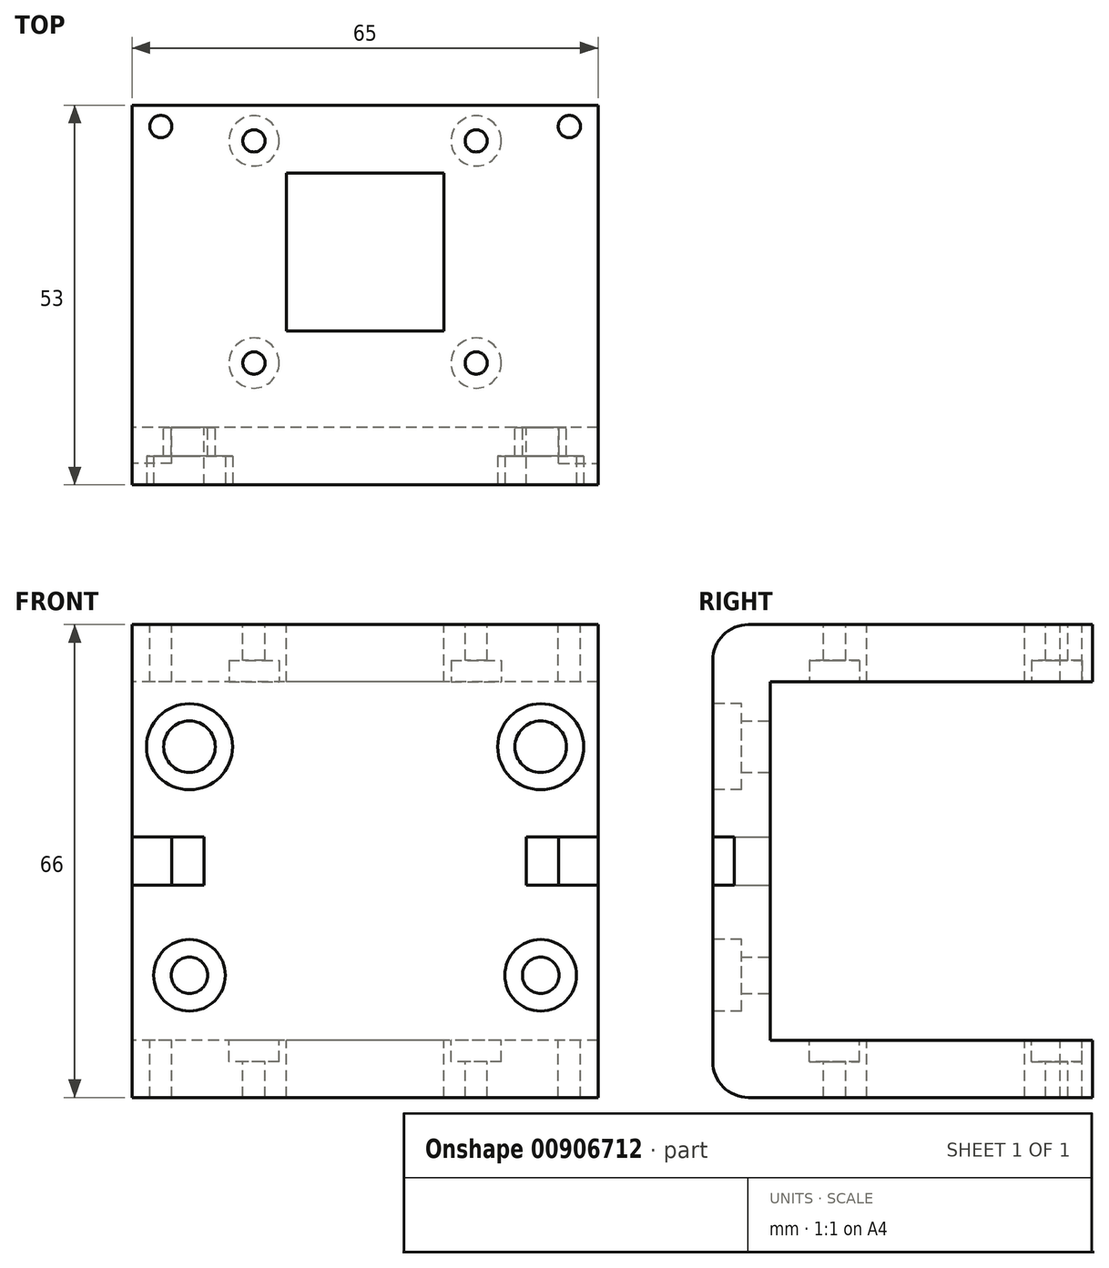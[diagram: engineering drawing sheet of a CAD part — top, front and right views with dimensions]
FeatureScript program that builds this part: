
annotation { "Feature Type Name" : "Feature", "Feature Type Description" : "" }
export const myFeature = defineFeature(function(context is Context, id is Id, definition is map)
    precondition{}
    {
        {
            var Q0;
            Q0=qCreatedBy(makeId("Front.planeOp"),FACE);
            var sketch = newSketch(context, id + "F0", { "sketchPlane" : qUnion([Q0])});
            skLineSegment(sketch, "E0.bottom", {"start": v(-32.5, 25) * mm, "end": v(32.5, 25) * mm});
            skLineSegment(sketch, "E0.top", {"start": v(-32.5, -25) * mm, "end": v(32.5, -25) * mm});
            skLineSegment(sketch, "E0.left", {"start": v(-32.5, 25) * mm, "end": v(-32.5, -25) * mm});
            skLineSegment(sketch, "E0.right", {"start": v(32.5, 25) * mm, "end": v(32.5, -25) * mm});
            skPoint(sketch, "E0.middle", {"position": v(0, 0) * mm});
            skLineSegment(sketch, "E1.bottom", {"start": v(-24.5, 15.95) * mm, "end": v(24.5, 15.95) * mm});
            skLineSegment(sketch, "E1.top", {"start": v(-24.5, -15.95) * mm, "end": v(24.5, -15.95) * mm});
            skLineSegment(sketch, "E1.left", {"start": v(-24.5, 15.95) * mm, "end": v(-24.5, -15.95) * mm});
            skLineSegment(sketch, "E1.right", {"start": v(24.5, 15.95) * mm, "end": v(24.5, -15.95) * mm});
            skCircle(sketch, "E2", {"center": v(-24.5, 15.95) * mm, "radius": 3.6 * mm});
            skCircle(sketch, "E3", {"center": v(24.5, 15.95) * mm, "radius": 3.6 * mm});
            skCircle(sketch, "E4", {"center": v(-24.5, -15.95) * mm, "radius": 2.55 * mm});
            skCircle(sketch, "E5", {"center": v(24.5, -15.95) * mm, "radius": 2.55 * mm});
            skLineSegment(sketch, "E6.bottom", {"start": v(-22.5, 3.35) * mm, "end": v(22.5, 3.35) * mm});
            skLineSegment(sketch, "E6.top", {"start": v(-22.5, -3.35) * mm, "end": v(22.5, -3.35) * mm});
            skLineSegment(sketch, "E6.left", {"start": v(-22.5, 3.35) * mm, "end": v(-22.5, -3.35) * mm});
            skLineSegment(sketch, "E6.right", {"start": v(22.5, 3.35) * mm, "end": v(22.5, -3.35) * mm});
            skLineSegment(sketch, "E7.bottom", {"start": v(-27, 3.35) * mm, "end": v(27, 3.35) * mm});
            skLineSegment(sketch, "E7.top", {"start": v(-27, -3.35) * mm, "end": v(27, -3.35) * mm});
            skLineSegment(sketch, "E7.left", {"start": v(-27, 3.35) * mm, "end": v(-27, -3.35) * mm});
            skLineSegment(sketch, "E7.right", {"start": v(27, 3.35) * mm, "end": v(27, -3.35) * mm});
            skSolve(sketch);
        }
        {
            var Q0;
            Q0=qSketchRegion(id+"F0",true);
            var Q1;
            {var subQ0=sQuery(id+"F0.wireOp",EDGE,"E2");var subQ1=sQuery(id+"F0.wireOp",EDGE,"E1.bottom");var subQ2=makeQuery(id+"F0.imprint","INTERSECT",VERTEX,{"derivedFrom":[subQ1,subQ0]});Q1=makeQuery(id+"F0.imprint","IMPRINT",FACE,{"disambiguationData":[TD([[makeQuery(id+"F0.imprint","IMPRINT",EDGE,{"disambiguationData":[TD([[subQ2,-1.0]])],"derivedFrom":subQ1}),-1.0]])]});}
            var Q2;
            {var subQ0=sQuery(id+"F0.wireOp",EDGE,"E4");var subQ1=sQuery(id+"F0.wireOp",EDGE,"E1.top");var subQ2=makeQuery(id+"F0.imprint","INTERSECT",VERTEX,{"derivedFrom":[subQ1,subQ0]});Q2=makeQuery(id+"F0.imprint","IMPRINT",FACE,{"disambiguationData":[TD([[makeQuery(id+"F0.imprint","IMPRINT",EDGE,{"disambiguationData":[TD([[subQ2,-1.0]])],"derivedFrom":subQ1}),1.0]])]});}
            var Q3;
            {var subQ5=sQuery(id+"F0.wireOp",EDGE,"E6.left");Q3=makeQuery(id+"F0.imprint","IMPRINT",FACE,{"disambiguationData":[TD([[makeQuery(id+"F0.imprint","IMPRINT",EDGE,{"derivedFrom":subQ5}),1.0]])]});}
            var Q4;
            {var subQ5=sQuery(id+"F0.wireOp",EDGE,"E6.right");Q4=makeQuery(id+"F0.imprint","IMPRINT",FACE,{"disambiguationData":[TD([[makeQuery(id+"F0.imprint","IMPRINT",EDGE,{"derivedFrom":subQ5}),-1.0]])]});}
            extrude(context, id + "F1", {"entities" : qUnion([Q0, Q1, Q2, Q3, Q4]), "depth" : 8 * mm, "offsetDistance" : 25 * mm});
        }
        {
            var Q0;
            Q0=makeQuery(id+"F1.opExtrude","CAP_FACE",FACE,{"disambiguationData":[OSD([sQuery(id+"F0.wireOp",EDGE,"E0.bottom"),sQuery(id+"F0.wireOp",EDGE,"E0.top"),sQuery(id+"F0.wireOp",EDGE,"E0.left"),sQuery(id+"F0.wireOp",EDGE,"E0.right"),sQuery(id+"F0.wireOp",EDGE,"E2"),sQuery(id+"F0.wireOp",EDGE,"E3"),sQuery(id+"F0.wireOp",EDGE,"E4"),sQuery(id+"F0.wireOp",EDGE,"E5"),sQuery(id+"F0.wireOp",EDGE,"E6.left"),sQuery(id+"F0.wireOp",EDGE,"E6.right"),sQuery(id+"F0.wireOp",EDGE,"E7.bottom"),sQuery(id+"F0.wireOp",EDGE,"E7.top"),sQuery(id+"F0.wireOp",EDGE,"E7.left"),sQuery(id+"F0.wireOp",EDGE,"E7.right")])],"isStart":false});
            var sketch = newSketch(context, id + "F2", { "sketchPlane" : qUnion([Q0])});
            skCircle(sketch, "E8", {"center": v(-24.5, 15.95) * mm, "radius": 6 * mm});
            skCircle(sketch, "E9", {"center": v(24.5, 15.95) * mm, "radius": 6 * mm});
            skCircle(sketch, "E10", {"center": v(-24.5, -15.95) * mm, "radius": 5 * mm});
            skCircle(sketch, "E11", {"center": v(24.5, -15.95) * mm, "radius": 5 * mm});
            skSolve(sketch);
        }
        {
            var Q0;
            Q0=makeQuery(id+"F2.imprint","IMPRINT",FACE,{"disambiguationData":[TD([[makeQuery(id+"F2.imprint","IMPRINT",EDGE,{"derivedFrom":sQuery(id+"F2.wireOp",EDGE,"E9")}),1.0]])]});
            var Q1;
            Q1=makeQuery(id+"F2.imprint","IMPRINT",FACE,{"disambiguationData":[TD([[makeQuery(id+"F2.imprint","IMPRINT",EDGE,{"derivedFrom":sQuery(id+"F2.wireOp",EDGE,"E8")}),1.0]])]});
            var Q2;
            Q2=makeQuery(id+"F2.imprint","IMPRINT",FACE,{"disambiguationData":[TD([[makeQuery(id+"F2.imprint","IMPRINT",EDGE,{"derivedFrom":sQuery(id+"F2.wireOp",EDGE,"E10")}),1.0]])]});
            var Q3;
            Q3=makeQuery(id+"F2.imprint","IMPRINT",FACE,{"disambiguationData":[TD([[makeQuery(id+"F2.imprint","IMPRINT",EDGE,{"derivedFrom":sQuery(id+"F2.wireOp",EDGE,"E11")}),1.0]])]});
            extrude(context, id + "F3", {"entities" : qUnion([Q0, Q1, Q2, Q3]), "operationType" : NewBodyOperationType.REMOVE, "oppositeDirection" : true, "depth" : 4 * mm, "offsetDistance" : 25 * mm});
        }
        {
            var Q0;
            Q0=makeQuery(id+"F1.opExtrude","CAP_FACE",FACE,{"disambiguationData":[OSD([sQuery(id+"F0.wireOp",EDGE,"E0.bottom"),sQuery(id+"F0.wireOp",EDGE,"E0.top"),sQuery(id+"F0.wireOp",EDGE,"E0.left"),sQuery(id+"F0.wireOp",EDGE,"E0.right"),sQuery(id+"F0.wireOp",EDGE,"E2"),sQuery(id+"F0.wireOp",EDGE,"E3"),sQuery(id+"F0.wireOp",EDGE,"E4"),sQuery(id+"F0.wireOp",EDGE,"E5"),sQuery(id+"F0.wireOp",EDGE,"E6.left"),sQuery(id+"F0.wireOp",EDGE,"E6.right"),sQuery(id+"F0.wireOp",EDGE,"E7.bottom"),sQuery(id+"F0.wireOp",EDGE,"E7.top"),sQuery(id+"F0.wireOp",EDGE,"E7.left"),sQuery(id+"F0.wireOp",EDGE,"E7.right")])],"isStart":false});
            var sketch = newSketch(context, id + "F4", { "sketchPlane" : qUnion([Q0])});
            skLineSegment(sketch, "E12.bottom", {"start": v(27, 3.35) * mm, "end": v(32.5, 3.35) * mm});
            skLineSegment(sketch, "E12.top", {"start": v(27, -3.35) * mm, "end": v(32.5, -3.35) * mm});
            skLineSegment(sketch, "E12.left", {"start": v(27, 3.35) * mm, "end": v(27, -3.35) * mm});
            skLineSegment(sketch, "E12.right", {"start": v(32.5, 3.35) * mm, "end": v(32.5, -3.35) * mm});
            skLineSegment(sketch, "E13.bottom", {"start": v(-27, 3.35) * mm, "end": v(-32.5, 3.35) * mm});
            skLineSegment(sketch, "E13.top", {"start": v(-27, -3.35) * mm, "end": v(-32.5, -3.35) * mm});
            skLineSegment(sketch, "E13.left", {"start": v(-27, 3.35) * mm, "end": v(-27, -3.35) * mm});
            skLineSegment(sketch, "E13.right", {"start": v(-32.5, 3.35) * mm, "end": v(-32.5, -3.35) * mm});
            skSolve(sketch);
        }
        {
            var Q0;
            Q0=qSketchRegion(id+"F4",true);
            extrude(context, id + "F5", {"entities" : qUnion([Q0]), "operationType" : NewBodyOperationType.REMOVE, "oppositeDirection" : true, "depth" : 3 * mm, "offsetDistance" : 25 * mm});
        }
        {
            var Q0;
            Q0=makeQuery(id+"F1.opExtrude","SWEPT_FACE",FACE,{"disambiguationData":[OSD([sQuery(id+"F0.wireOp",EDGE,"E0.top")])]});
            extrude(context, id + "F6", {"entities" : qUnion([Q0]), "operationType" : NewBodyOperationType.ADD, "depth" : 8 * mm, "offsetDistance" : 25 * mm});
        }
        {
            var Q0;
            Q0=makeQuery(id+"F1.opExtrude","SWEPT_FACE",FACE,{"disambiguationData":[OSD([sQuery(id+"F0.wireOp",EDGE,"E0.bottom")])]});
            extrude(context, id + "F7", {"entities" : qUnion([Q0]), "operationType" : NewBodyOperationType.ADD, "depth" : 8 * mm, "offsetDistance" : 25 * mm});
        }
        {
            var Q0;
            {var subQ0=sQuery(id+"F0.wireOp",EDGE,"E0.bottom");var subQ1=sQuery(id+"F0.wireOp",EDGE,"E0.top");Q0=makeQuery(id+"F7.boolean.opBoolean","MERGE",FACE,{"derivedFrom":[makeQuery(id+"F6.boolean.opBoolean","MERGE",FACE,{"derivedFrom":[makeQuery(id+"F1.opExtrude","CAP_FACE",FACE,{"disambiguationData":[OSD([subQ0,subQ1,sQuery(id+"F0.wireOp",EDGE,"E0.left"),sQuery(id+"F0.wireOp",EDGE,"E0.right"),sQuery(id+"F0.wireOp",EDGE,"E2"),sQuery(id+"F0.wireOp",EDGE,"E3"),sQuery(id+"F0.wireOp",EDGE,"E4"),sQuery(id+"F0.wireOp",EDGE,"E5"),sQuery(id+"F0.wireOp",EDGE,"E6.left"),sQuery(id+"F0.wireOp",EDGE,"E6.right"),sQuery(id+"F0.wireOp",EDGE,"E7.bottom"),sQuery(id+"F0.wireOp",EDGE,"E7.top"),sQuery(id+"F0.wireOp",EDGE,"E7.left"),sQuery(id+"F0.wireOp",EDGE,"E7.right")])],"isStart":true}),makeQuery(id+"F6.opExtrude","SWEPT_FACE",FACE,{"disambiguationData":[OSD([subQ1]),TDD([makeQuery(id+"F1.opExtrude","CAP_EDGE",EDGE,{"disambiguationData":[OSD([subQ1])],"isStart":true})])]})]}),makeQuery(id+"F7.opExtrude","SWEPT_FACE",FACE,{"disambiguationData":[OSD([subQ0]),TDD([makeQuery(id+"F1.opExtrude","CAP_EDGE",EDGE,{"disambiguationData":[OSD([subQ0])],"isStart":true})])]})]});}
            var sketch = newSketch(context, id + "F8", { "sketchPlane" : qUnion([Q0])});
            skLineSegment(sketch, "E14.bottom", {"start": v(-32.5, 33) * mm, "end": v(32.5, 33) * mm});
            skLineSegment(sketch, "E14.top", {"start": v(-32.5, 25) * mm, "end": v(32.5, 25) * mm});
            skLineSegment(sketch, "E14.left", {"start": v(-32.5, 33) * mm, "end": v(-32.5, 25) * mm});
            skLineSegment(sketch, "E14.right", {"start": v(32.5, 33) * mm, "end": v(32.5, 25) * mm});
            skLineSegment(sketch, "E15.bottom", {"start": v(-32.5, -33) * mm, "end": v(32.5, -33) * mm});
            skLineSegment(sketch, "E15.top", {"start": v(-32.5, -25) * mm, "end": v(32.5, -25) * mm});
            skLineSegment(sketch, "E15.left", {"start": v(-32.5, -33) * mm, "end": v(-32.5, -25) * mm});
            skLineSegment(sketch, "E15.right", {"start": v(32.5, -33) * mm, "end": v(32.5, -25) * mm});
            skSolve(sketch);
        }
        {
            var Q0;
            Q0 = qSketchRegion(id + "F8", true);
            extrude(context, id + "F9", {"entities" : qUnion([Q0]), "operationType" : NewBodyOperationType.ADD, "depth" : 45 * mm, "offsetDistance" : 25 * mm});
        }
        {
            var Q0;
            Q0=makeQuery(id+"F9.boolean.opBoolean","MERGE",FACE,{"derivedFrom":[makeQuery(id+"F7.opExtrude","CAP_FACE",FACE,{"disambiguationData":[OSD([sQuery(id+"F0.wireOp",EDGE,"E0.bottom")])],"isStart":false}),makeQuery(id+"F9.opExtrude","SWEPT_FACE",FACE,{"disambiguationData":[OSD([sQuery(id+"F8.wireOp",EDGE,"E14.bottom")])]})]});
            var sketch = newSketch(context, id + "F10", { "sketchPlane" : qUnion([Q0])});
            skLineSegment(sketch, "E16.bottom", {"start": v(-32.5, 45) * mm, "end": v(32.5, 45) * mm});
            skLineSegment(sketch, "E16.top", {"start": v(-32.5, 4) * mm, "end": v(32.5, 4) * mm});
            skLineSegment(sketch, "E16.left", {"start": v(-32.5, 45) * mm, "end": v(-32.5, 4) * mm});
            skLineSegment(sketch, "E16.right", {"start": v(32.5, 45) * mm, "end": v(32.5, 4) * mm});
            skLineSegment(sketch, "E17.bottom", {"start": v(15.5, 9) * mm, "end": v(-15.5, 9) * mm});
            skLineSegment(sketch, "E17.top", {"start": v(15.5, 40) * mm, "end": v(-15.5, 40) * mm});
            skLineSegment(sketch, "E17.left", {"start": v(15.5, 9) * mm, "end": v(15.5, 40) * mm});
            skLineSegment(sketch, "E17.right", {"start": v(-15.5, 9) * mm, "end": v(-15.5, 40) * mm});
            skPoint(sketch, "E17.middle", {"position": v(0, 24.5) * mm});
            skPoint(sketch, "E17.middle.positionSnap0", {"position": v(-32.5, 24.5) * mm});
            skPoint(sketch, "E17.middle.positionSnap1", {"position": v(0, 4) * mm});
            skPoint(sketch, "E17.centerSnap0", {"position": v(-32.5, 24.5) * mm});
            skPoint(sketch, "E17.centerSnap1", {"position": v(0, 4) * mm});
            skCircle(sketch, "E18", {"center": v(15.5, 9) * mm, "radius": 1.55 * mm});
            skCircle(sketch, "E19", {"center": v(-15.5, 9) * mm, "radius": 1.55 * mm});
            skCircle(sketch, "E20", {"center": v(15.5, 40) * mm, "radius": 1.55 * mm});
            skCircle(sketch, "E21", {"center": v(-15.5, 40) * mm, "radius": 1.55 * mm});
            skLineSegment(sketch, "E22.bottom", {"start": v(11, 13.5) * mm, "end": v(-11, 13.5) * mm});
            skLineSegment(sketch, "E22.top", {"start": v(11, 35.5) * mm, "end": v(-11, 35.5) * mm});
            skLineSegment(sketch, "E22.left", {"start": v(11, 13.5) * mm, "end": v(11, 35.5) * mm});
            skLineSegment(sketch, "E22.right", {"start": v(-11, 13.5) * mm, "end": v(-11, 35.5) * mm});
            skLineSegment(sketch, "E23", {"start": v(32.5, 45) * mm, "end": v(32.5, 42) * mm});
            skLineSegment(sketch, "E24", {"start": v(32.5, 42) * mm, "end": v(28.5, 42) * mm});
            skCircle(sketch, "E25", {"center": v(28.5, 42) * mm, "radius": 1.55 * mm});
            skLineSegment(sketch, "E26", {"start": v(-32.5, 45) * mm, "end": v(-32.5, 42) * mm});
            skLineSegment(sketch, "E27", {"start": v(-32.5, 42) * mm, "end": v(-28.5, 42) * mm});
            skCircle(sketch, "E28", {"center": v(-28.5, 42) * mm, "radius": 1.55 * mm});
            skSolve(sketch);
        }
        {
            var Q0;
            {var subQ0=sQuery(id+"F10.wireOp",EDGE,"E17.left");var subQ1=sQuery(id+"F10.wireOp",EDGE,"E17.bottom");var subQ2=makeQuery(id+"F10.imprint","INTERSECT",VERTEX,{"derivedFrom":[subQ1,subQ0]});Q0=makeQuery(id+"F10.imprint","IMPRINT",FACE,{"disambiguationData":[TD([[makeQuery(id+"F10.imprint","IMPRINT",EDGE,{"disambiguationData":[TD([[subQ2,-1.0]])],"derivedFrom":subQ1}),1.0]])]});}
            var Q1;
            {var subQ0=sQuery(id+"F10.wireOp",EDGE,"E17.left");var subQ1=sQuery(id+"F10.wireOp",EDGE,"E17.bottom");var subQ2=makeQuery(id+"F10.imprint","INTERSECT",VERTEX,{"derivedFrom":[subQ1,subQ0]});Q1=makeQuery(id+"F10.imprint","IMPRINT",FACE,{"disambiguationData":[TD([[makeQuery(id+"F10.imprint","IMPRINT",EDGE,{"disambiguationData":[TD([[subQ2,-1.0]])],"derivedFrom":subQ1}),-1.0]])]});}
            var Q2;
            {var subQ0=sQuery(id+"F10.wireOp",EDGE,"E17.right");var subQ1=sQuery(id+"F10.wireOp",EDGE,"E17.bottom");var subQ2=makeQuery(id+"F10.imprint","INTERSECT",VERTEX,{"derivedFrom":[subQ1,subQ0]});Q2=makeQuery(id+"F10.imprint","IMPRINT",FACE,{"disambiguationData":[TD([[makeQuery(id+"F10.imprint","IMPRINT",EDGE,{"disambiguationData":[TD([[subQ2,1.0]])],"derivedFrom":subQ1}),1.0]])]});}
            var Q3;
            {var subQ0=sQuery(id+"F10.wireOp",EDGE,"E17.right");var subQ1=sQuery(id+"F10.wireOp",EDGE,"E17.bottom");var subQ2=makeQuery(id+"F10.imprint","INTERSECT",VERTEX,{"derivedFrom":[subQ1,subQ0]});Q3=makeQuery(id+"F10.imprint","IMPRINT",FACE,{"disambiguationData":[TD([[makeQuery(id+"F10.imprint","IMPRINT",EDGE,{"disambiguationData":[TD([[subQ2,1.0]])],"derivedFrom":subQ1}),-1.0]])]});}
            var Q4;
            {var subQ0=sQuery(id+"F10.wireOp",EDGE,"E17.left");var subQ1=sQuery(id+"F10.wireOp",EDGE,"E17.top");var subQ2=makeQuery(id+"F10.imprint","INTERSECT",VERTEX,{"derivedFrom":[subQ1,subQ0]});Q4=makeQuery(id+"F10.imprint","IMPRINT",FACE,{"disambiguationData":[TD([[makeQuery(id+"F10.imprint","IMPRINT",EDGE,{"disambiguationData":[TD([[subQ2,-1.0]])],"derivedFrom":subQ1}),-1.0]])]});}
            var Q5;
            {var subQ0=sQuery(id+"F10.wireOp",EDGE,"E17.left");var subQ1=sQuery(id+"F10.wireOp",EDGE,"E17.top");var subQ2=makeQuery(id+"F10.imprint","INTERSECT",VERTEX,{"derivedFrom":[subQ1,subQ0]});Q5=makeQuery(id+"F10.imprint","IMPRINT",FACE,{"disambiguationData":[TD([[makeQuery(id+"F10.imprint","IMPRINT",EDGE,{"disambiguationData":[TD([[subQ2,-1.0]])],"derivedFrom":subQ1}),1.0]])]});}
            var Q6;
            {var subQ0=sQuery(id+"F10.wireOp",EDGE,"E17.right");var subQ1=sQuery(id+"F10.wireOp",EDGE,"E17.top");var subQ2=makeQuery(id+"F10.imprint","INTERSECT",VERTEX,{"derivedFrom":[subQ1,subQ0]});Q6=makeQuery(id+"F10.imprint","IMPRINT",FACE,{"disambiguationData":[TD([[makeQuery(id+"F10.imprint","IMPRINT",EDGE,{"disambiguationData":[TD([[subQ2,1.0]])],"derivedFrom":subQ1}),-1.0]])]});}
            var Q7;
            {var subQ0=sQuery(id+"F10.wireOp",EDGE,"E17.right");var subQ1=sQuery(id+"F10.wireOp",EDGE,"E17.top");var subQ2=makeQuery(id+"F10.imprint","INTERSECT",VERTEX,{"derivedFrom":[subQ1,subQ0]});Q7=makeQuery(id+"F10.imprint","IMPRINT",FACE,{"disambiguationData":[TD([[makeQuery(id+"F10.imprint","IMPRINT",EDGE,{"disambiguationData":[TD([[subQ2,1.0]])],"derivedFrom":subQ1}),1.0]])]});}
            var Q8;
            Q8=makeQuery(id+"F10.imprint","IMPRINT",FACE,{"disambiguationData":[TD([[makeQuery(id+"F10.imprint","IMPRINT",EDGE,{"derivedFrom":sQuery(id+"F10.wireOp",EDGE,"E22.bottom")}),-1.0]])]});
            var Q9;
            Q9=makeQuery(id+"F10.imprint","IMPRINT",FACE,{"disambiguationData":[TD([[makeQuery(id+"F10.imprint","IMPRINT",EDGE,{"derivedFrom":sQuery(id+"F10.wireOp",EDGE,"E25")}),1.0]])]});
            var Q10;
            Q10=makeQuery(id+"F10.imprint","IMPRINT",FACE,{"disambiguationData":[TD([[makeQuery(id+"F10.imprint","IMPRINT",EDGE,{"derivedFrom":sQuery(id+"F10.wireOp",EDGE,"E28")}),1.0]])]});
            extrude(context, id + "F11", {"entities" : qUnion([Q0, Q1, Q2, Q3, Q4, Q5, Q6, Q7, Q8, Q9, Q10]), "operationType" : NewBodyOperationType.REMOVE, "oppositeDirection" : true, "depth" : 100 * mm, "offsetDistance" : 25 * mm});
        }
        {
            var Q0;
            Q0=makeQuery(id+"F9.opExtrude","SWEPT_FACE",FACE,{"disambiguationData":[OSD([sQuery(id+"F8.wireOp",EDGE,"E14.top")])]});
            var sketch = newSketch(context, id + "F12", { "sketchPlane" : qUnion([Q0])});
            skCircle(sketch, "E29", {"center": v(-15.5, -40) * mm, "radius": 3.5 * mm});
            skCircle(sketch, "E30", {"center": v(-15.5, -9) * mm, "radius": 3.5 * mm});
            skCircle(sketch, "E31", {"center": v(15.5, -9) * mm, "radius": 3.5 * mm});
            skCircle(sketch, "E32", {"center": v(15.5, -40) * mm, "radius": 3.5 * mm});
            skSolve(sketch);
        }
        {
            var Q0;
            Q0=makeQuery(id+"F12.imprint","IMPRINT",FACE,{"disambiguationData":[TD([[makeQuery(id+"F12.imprint","IMPRINT",EDGE,{"derivedFrom":sQuery(id+"F12.wireOp",EDGE,"E29")}),1.0]])]});
            var Q1;
            Q1=makeQuery(id+"F12.imprint","IMPRINT",FACE,{"disambiguationData":[TD([[makeQuery(id+"F12.imprint","IMPRINT",EDGE,{"derivedFrom":sQuery(id+"F12.wireOp",EDGE,"E30")}),1.0]])]});
            var Q2;
            Q2=makeQuery(id+"F12.imprint","IMPRINT",FACE,{"disambiguationData":[TD([[makeQuery(id+"F12.imprint","IMPRINT",EDGE,{"derivedFrom":sQuery(id+"F12.wireOp",EDGE,"E31")}),1.0]])]});
            var Q3;
            Q3=makeQuery(id+"F12.imprint","IMPRINT",FACE,{"disambiguationData":[TD([[makeQuery(id+"F12.imprint","IMPRINT",EDGE,{"derivedFrom":sQuery(id+"F12.wireOp",EDGE,"E32")}),1.0]])]});
            extrude(context, id + "F13", {"entities" : qUnion([Q0, Q1, Q2, Q3]), "operationType" : NewBodyOperationType.REMOVE, "oppositeDirection" : true, "depth" : 3 * mm, "offsetDistance" : 25 * mm});
        }
        {
            var Q0;
            Q0=makeQuery(id+"F9.opExtrude","SWEPT_FACE",FACE,{"disambiguationData":[OSD([sQuery(id+"F8.wireOp",EDGE,"E15.top")])]});
            var sketch = newSketch(context, id + "F14", { "sketchPlane" : qUnion([Q0])});
            skCircle(sketch, "E33", {"center": v(15.5, 40) * mm, "radius": 3.5 * mm});
            skCircle(sketch, "E34", {"center": v(15.5, 9) * mm, "radius": 3.5 * mm});
            skCircle(sketch, "E35", {"center": v(-15.5, 9) * mm, "radius": 3.5 * mm});
            skCircle(sketch, "E36", {"center": v(-15.5, 40) * mm, "radius": 3.5 * mm});
            skSolve(sketch);
        }
        {
            var Q0;
            Q0=makeQuery(id+"F14.imprint","IMPRINT",FACE,{"disambiguationData":[TD([[makeQuery(id+"F14.imprint","IMPRINT",EDGE,{"derivedFrom":sQuery(id+"F14.wireOp",EDGE,"E34")}),1.0]])]});
            var Q1;
            Q1=makeQuery(id+"F14.imprint","IMPRINT",FACE,{"disambiguationData":[TD([[makeQuery(id+"F14.imprint","IMPRINT",EDGE,{"derivedFrom":sQuery(id+"F14.wireOp",EDGE,"E33")}),1.0]])]});
            var Q2;
            Q2=makeQuery(id+"F14.imprint","IMPRINT",FACE,{"disambiguationData":[TD([[makeQuery(id+"F14.imprint","IMPRINT",EDGE,{"derivedFrom":sQuery(id+"F14.wireOp",EDGE,"E36")}),1.0]])]});
            var Q3;
            Q3=makeQuery(id+"F14.imprint","IMPRINT",FACE,{"disambiguationData":[TD([[makeQuery(id+"F14.imprint","IMPRINT",EDGE,{"derivedFrom":sQuery(id+"F14.wireOp",EDGE,"E35")}),1.0]])]});
            extrude(context, id + "F15", {"entities" : qUnion([Q0, Q1, Q2, Q3]), "operationType" : NewBodyOperationType.REMOVE, "oppositeDirection" : true, "depth" : 3 * mm, "offsetDistance" : 25 * mm});
        }
        {
            var Q0;
            {var subQ0=sQuery(id+"F0.wireOp",EDGE,"E0.top");Q0=makeQuery(id+"F6.opExtrude","CAP_EDGE",EDGE,{"disambiguationData":[OSD([subQ0]),TDD([makeQuery(id+"F1.opExtrude","CAP_EDGE",EDGE,{"disambiguationData":[OSD([subQ0])],"isStart":false})])],"isStart":false});}
            var Q1;
            {var subQ0=sQuery(id+"F0.wireOp",EDGE,"E0.bottom");Q1=makeQuery(id+"F7.opExtrude","CAP_EDGE",EDGE,{"disambiguationData":[OSD([subQ0]),TDD([makeQuery(id+"F1.opExtrude","CAP_EDGE",EDGE,{"disambiguationData":[OSD([subQ0])],"isStart":false})])],"isStart":false});}
            fillet(context, id + "F16", {"entities" : qUnion([Q0, Q1]), "radius" : 5 * mm, "tangentPropagation" : true, "allowEdgeOverflow" : false});
        }
    });
